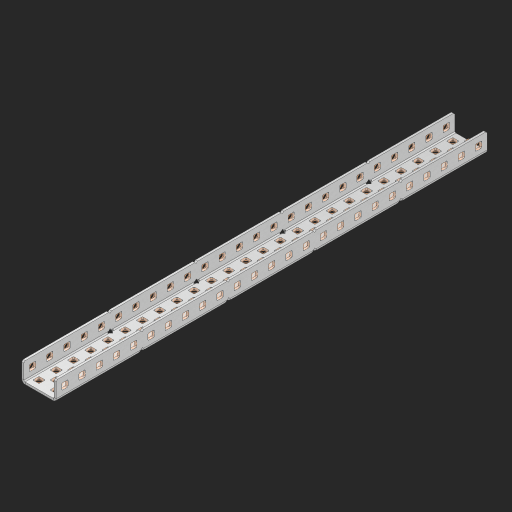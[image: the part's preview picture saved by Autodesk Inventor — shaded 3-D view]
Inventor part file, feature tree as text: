
AUTODESK INVENTOR PART (.ipt)
format: ipt  version: 2023 (Build 270158000, 158)  size: 1,622,016 bytes
history: native  units: in
note: dims shown in document units (in); Inventor stores cm internally (conversion verified against a paired STEP export)
features: other x132, extrude x123, sheet_metal_op x11, sketch x10, pattern_linear x2, mirror x1, chamfer x1
ambient origin geometry x8: Origin, YZ Plane, XZ Plane, XY Plane, X Axis, Y Axis, Z Axis, Center Point
bodies: Solid1 (feature_tree), Body (feature_tree)
feature tree (280):
  sheet_metal_op  "Flanges"
  other  "Flange Pattern Plane"
  other  "Flange Pattern Sketch"
  sheet_metal_op  "Flange Pattern"
  sheet_metal_op  "Body Pattern"
  pattern_linear  "Center Pattern"  Spacing1=0.0625in  [1 undecoded]
  other  "Arc Length"
  mirror  "Notch Mirror"
  pattern_linear  "Notch Pattern"  Spacing1=0.182in  [1 undecoded]
  chamfer  "End Chamfer"
  extrude  "Half Cut"  Depth=0.02in
  sketch  "Sketch1"  dims[d0=1.0in]
  other  "Plate1"
  sketch  "Sketch2"  dims[d1=12.5in]
  other  "Plate2"
  sheet_metal_op  "Bend1"
  sheet_metal_op  "Corner1"
  sketch  "Sketch3"  dims[d2=0.0625in]
  sketch  "Sketch7"  dims[d3=0.0625in]
  other  "Srf1"
  other  "Srf2"
  sketch  "Sketch8"  dims[d4=0.0312in]
  sketch  "Sketch9"  dims[d5=0.125in]
  other  "Srf91"
  sheet_metal_op  "Body Pattern Sketch"
  other  "Srf92"
  sketch  "Sketch13"  dims[d6=0.0625in]
  sketch  "Sketch14"  dims[d7=0.5in d8=90.0deg d9=0.0312in]
  sketch  "Sketch15"  dims[d10=0.25in]
  sketch  "Sketch16"  dims[d11=0.0625in d12=0.0625in d16=0.182in d17=0.02in d18=0.0625in d19=0.0in d20=0.25in d21=0.25in d38=9.8425in d40=0.5in d41=0.7874in d43=1.0in d46=0.172in d47=1.0in d48=0.0in d49=0.182in d50=0.02in d51=0.25in d52=0.25in d53=0.0625in d54=0.0in d55=0.172in d56=1.0in d57=0.0in d58=0.25in d60=9.8425in d62=0.5in d63=0.7874in d65=0.5in d85=0.1473in d86=0.1782in d88=0.04in d89=0.0625in d90=0.0in d91=0.04in d92=0.0491in d95=2.5in d96=0.04in d97=0.25in d98=45.0deg d99=0.25in d100=0.5in d101=0.0in d102=2.497in d106=0.182in d107=0.02in d108=0.5in d109=0.5in d110=0.0625in d111=0.0in d112=0.172in d113=0.5in d114=0.0in d117=0.5in d118=0.5in d119=0.5in]
  other  "Srf786"
  other  "Srf823"
  other  "Srf824"
  other  "Srf825"
  other  "Srf826"
  other  "Srf827"
  other  "Srf828"
  other  "Srf829"
  other  "Srf856"
  other  "Srf857"
  other  "Srf858"
  other  "Srf859"
  other  "Srf860"
  other  "Srf861"
  other  "Srf862"
  other  "Srf889"
  other  "Srf890"
  other  "Srf891"
  other  "Srf892"
  other  "Srf893"
  other  "Srf894"
  other  "Srf895"
  other  "Srf896"
  other  "Srf922"
  other  "Srf923"
  other  "Srf924"
  other  "Srf925"
  other  "Srf926"
  other  "Srf959"
  other  "Srf960"
  other  "Srf961"
  other  "Srf962"
  other  "Srf963"
  other  "Srf996"
  other  "Srf997"
  other  "Srf998"
  other  "Srf999"
  other  "Srf1000"
  other  "Srf1143"
  other  "Srf1144"
  other  "Srf1145"
  other  "Srf1146"
  other  "Srf1147"
  other  "Srf1148"
  other  "Srf1149"
  other  "Srf1150"
  other  "Srf1151"
  other  "Srf1152"
  other  "Srf1153"
  other  "Srf1154"
  other  "Srf1155"
  other  "Srf1156"
  other  "Srf1157"
  other  "Srf1158"
  other  "Srf1159"
  other  "Srf1160"
  other  "Srf1161"
  other  "Srf1162"
  other  "Srf1163"
  other  "Srf1164"
  other  "Srf1165"
  other  "Srf1166"
  other  "Srf1167"
  other  "Srf1168"
  other  "Srf1169"
  other  "Srf1170"
  other  "Srf1171"
  other  "Srf1172"
  other  "Srf1173"
  other  "Srf1174"
  other  "Srf1175"
  other  "Srf1176"
  other  "Srf1177"
  other  "Srf1178"
  other  "Srf1199"
  other  "Srf1200"
  other  "Srf1201"
  other  "Srf1202"
  other  "Srf1203"
  other  "Srf1204"
  other  "Srf1205"
  other  "Srf1206"
  other  "Srf1207"
  other  "Srf1208"
  other  "Srf1209"
  other  "Srf1210"
  other  "Srf1211"
  other  "Srf1212"
  other  "Srf1213"
  other  "Srf1214"
  other  "Srf1215"
  other  "Srf1216"
  other  "Srf1217"
  other  "Srf1218"
  other  "Srf1219"
  other  "Srf1220"
  other  "Srf1221"
  other  "Srf1222"
  other  "Srf1223"
  other  "Srf1224"
  other  "Srf1225"
  other  "Srf1226"
  other  "Srf1227"
  other  "Srf1228"
  other  "Srf1229"
  other  "Srf1230"
  other  "Srf1231"
  other  "Srf1232"
  other  "Srf1233"
  other  "Srf1234"
  other  "Srf1255"
  other  "Srf1256"
  other  "Srf1257"
  other  "Srf1258"
  other  "Srf1259"
  other  "Srf1260"
  other  "Srf1261"
  other  "Srf1262"
  other  "Srf1263"
  other  "Srf1264"
  other  "Srf1265"
  sheet_metal_op  "Flange Stamp"
  sheet_metal_op  "Flange Circle"
  sheet_metal_op  "Body Stamp"
  sheet_metal_op  "Body Circle"
  other  "Center Stamp"
  other  "Center Circle"
  sheet_metal_op  "Notch"
  extrude  "ExtrusionSrf2"  Depth=0.0625in
  extrude  "ExtrusionSrf92"  TaperAngle=0.0deg  [1 undecoded]
  extrude  "ExtrusionSrf823"  Depth=0.5in
  extrude  "ExtrusionSrf824"  Depth=0.5in
  extrude  "ExtrusionSrf825"  Depth=0.5in
  extrude  "ExtrusionSrf826"  Depth=0.5in
  extrude  "ExtrusionSrf827"  Depth=1.0in TaperAngle=0.0deg
  extrude  "ExtrusionSrf828"  Depth=0.5in
  extrude  "ExtrusionSrf829"  Depth=0.02in
  extrude  "ExtrusionSrf856"  Depth=0.5in
  extrude  "ExtrusionSrf857"  Depth=0.5in
  extrude  "ExtrusionSrf858"  Depth=0.0625in
  extrude  "ExtrusionSrf859"  TaperAngle=0.0deg  [1 undecoded]
  extrude  "ExtrusionSrf860"  Depth=0.5in
  extrude  "ExtrusionSrf861"  Depth=1.0in TaperAngle=0.0deg
  extrude  "ExtrusionSrf862"  Depth=0.5in
  extrude  "ExtrusionSrf889"  Depth=0.5in
  extrude  "ExtrusionSrf890"  Depth=0.5in
  extrude  "ExtrusionSrf891"  Depth=0.5in
  extrude  "ExtrusionSrf892"  Depth=0.5in
  extrude  "ExtrusionSrf893"  Depth=0.5in
  extrude  "ExtrusionSrf894"  Depth=0.0625in
  extrude  "ExtrusionSrf895"  TaperAngle=0.0deg  [1 undecoded]
  extrude  "ExtrusionSrf896"  Depth=0.5in
  extrude  "ExtrusionSrf922"  Depth=0.5in
  extrude  "ExtrusionSrf923"  Depth=2.5in
  extrude  "ExtrusionSrf924"  Depth=0.5in TaperAngle=45.0deg
  extrude  "ExtrusionSrf925"  Depth=0.5in
  extrude  "ExtrusionSrf926"  Depth=0.5in TaperAngle=0.0deg
  extrude  "ExtrusionSrf959"  Depth=0.5in
  extrude  "ExtrusionSrf960"  Depth=0.5in
  extrude  "ExtrusionSrf961"  Depth=0.02in
  extrude  "ExtrusionSrf962"  Depth=0.5in
  extrude  "ExtrusionSrf963"  Depth=0.5in
  extrude  "ExtrusionSrf996"  Depth=0.0625in
  extrude  "ExtrusionSrf997"  TaperAngle=0.0deg  [1 undecoded]
  extrude  "ExtrusionSrf998"  Depth=0.5in
  extrude  "ExtrusionSrf999"  Depth=0.5in TaperAngle=0.0deg
  extrude  "ExtrusionSrf1000"  Depth=0.5in
  extrude  "ExtrusionSrf1143"  Depth=0.5in
  extrude  "ExtrusionSrf1144"  Depth=0.5in
  extrude  "ExtrusionSrf1145"  [1 undecoded]
  extrude  "ExtrusionSrf1146"  [1 undecoded]
  extrude  "ExtrusionSrf1147"  [1 undecoded]
  extrude  "ExtrusionSrf1148"  [1 undecoded]
  extrude  "ExtrusionSrf1149"  [1 undecoded]
  extrude  "ExtrusionSrf1150"  [1 undecoded]
  extrude  "ExtrusionSrf1151"  [1 undecoded]
  extrude  "ExtrusionSrf1152"  [1 undecoded]
  extrude  "ExtrusionSrf1153"  [1 undecoded]
  extrude  "ExtrusionSrf1154"  [1 undecoded]
  extrude  "ExtrusionSrf1155"  [1 undecoded]
  extrude  "ExtrusionSrf1156"  [1 undecoded]
  extrude  "ExtrusionSrf1157"  [1 undecoded]
  extrude  "ExtrusionSrf1158"  [1 undecoded]
  extrude  "ExtrusionSrf1159"  [1 undecoded]
  extrude  "ExtrusionSrf1160"  [1 undecoded]
  extrude  "ExtrusionSrf1161"  [1 undecoded]
  extrude  "ExtrusionSrf1162"  [1 undecoded]
  extrude  "ExtrusionSrf1163"  [1 undecoded]
  extrude  "ExtrusionSrf1164"  [1 undecoded]
  extrude  "ExtrusionSrf1165"  [1 undecoded]
  extrude  "ExtrusionSrf1166"  [1 undecoded]
  extrude  "ExtrusionSrf1167"  [1 undecoded]
  extrude  "ExtrusionSrf1168"  [1 undecoded]
  extrude  "ExtrusionSrf1169"  [1 undecoded]
  extrude  "ExtrusionSrf1170"  [1 undecoded]
  extrude  "ExtrusionSrf1171"  [1 undecoded]
  extrude  "ExtrusionSrf1172"  [1 undecoded]
  extrude  "ExtrusionSrf1173"  [1 undecoded]
  extrude  "ExtrusionSrf1174"  [1 undecoded]
  extrude  "ExtrusionSrf1175"  [1 undecoded]
  extrude  "ExtrusionSrf1176"  [1 undecoded]
  extrude  "ExtrusionSrf1177"  [1 undecoded]
  extrude  "ExtrusionSrf1178"  [1 undecoded]
  extrude  "ExtrusionSrf1199"  [1 undecoded]
  extrude  "ExtrusionSrf1200"  [1 undecoded]
  extrude  "ExtrusionSrf1201"  [1 undecoded]
  extrude  "ExtrusionSrf1202"  [1 undecoded]
  extrude  "ExtrusionSrf1203"  [1 undecoded]
  extrude  "ExtrusionSrf1204"  [1 undecoded]
  extrude  "ExtrusionSrf1205"  [1 undecoded]
  extrude  "ExtrusionSrf1206"  [1 undecoded]
  extrude  "ExtrusionSrf1207"  [1 undecoded]
  extrude  "ExtrusionSrf1208"  [1 undecoded]
  extrude  "ExtrusionSrf1209"  [1 undecoded]
  extrude  "ExtrusionSrf1210"  [1 undecoded]
  extrude  "ExtrusionSrf1211"  [1 undecoded]
  extrude  "ExtrusionSrf1212"  [1 undecoded]
  extrude  "ExtrusionSrf1213"  [1 undecoded]
  extrude  "ExtrusionSrf1214"  [1 undecoded]
  extrude  "ExtrusionSrf1215"  [1 undecoded]
  extrude  "ExtrusionSrf1216"  [1 undecoded]
  extrude  "ExtrusionSrf1217"  [1 undecoded]
  extrude  "ExtrusionSrf1218"  [1 undecoded]
  extrude  "ExtrusionSrf1219"  [1 undecoded]
  extrude  "ExtrusionSrf1220"  [1 undecoded]
  extrude  "ExtrusionSrf1221"  [1 undecoded]
  extrude  "ExtrusionSrf1222"  [1 undecoded]
  extrude  "ExtrusionSrf1223"  [1 undecoded]
  extrude  "ExtrusionSrf1224"  [1 undecoded]
  extrude  "ExtrusionSrf1225"  [1 undecoded]
  extrude  "ExtrusionSrf1226"  [1 undecoded]
  extrude  "ExtrusionSrf1227"  [1 undecoded]
  extrude  "ExtrusionSrf1228"  [1 undecoded]
  extrude  "ExtrusionSrf1229"  [1 undecoded]
  extrude  "ExtrusionSrf1230"  [1 undecoded]
  extrude  "ExtrusionSrf1231"  [1 undecoded]
  extrude  "ExtrusionSrf1232"  [1 undecoded]
  extrude  "ExtrusionSrf1233"  [1 undecoded]
  extrude  "ExtrusionSrf1234"  [1 undecoded]
  extrude  "ExtrusionSrf1255"  [1 undecoded]
  extrude  "ExtrusionSrf1256"  [1 undecoded]
  extrude  "ExtrusionSrf1257"  [1 undecoded]
  extrude  "ExtrusionSrf1258"  [1 undecoded]
  extrude  "ExtrusionSrf1259"  [1 undecoded]
  extrude  "ExtrusionSrf1260"  [1 undecoded]
  extrude  "ExtrusionSrf1261"  [1 undecoded]
  extrude  "ExtrusionSrf1262"  [1 undecoded]
  extrude  "ExtrusionSrf1263"  [1 undecoded]
  extrude  "ExtrusionSrf1264"  [1 undecoded]
  extrude  "ExtrusionSrf1265"  [1 undecoded]
note: 87 required parameter values undecoded (feature->parameter linkage not recoverable at this tier; creation-order binding heuristic only, values carry confidence <= 0.55)
